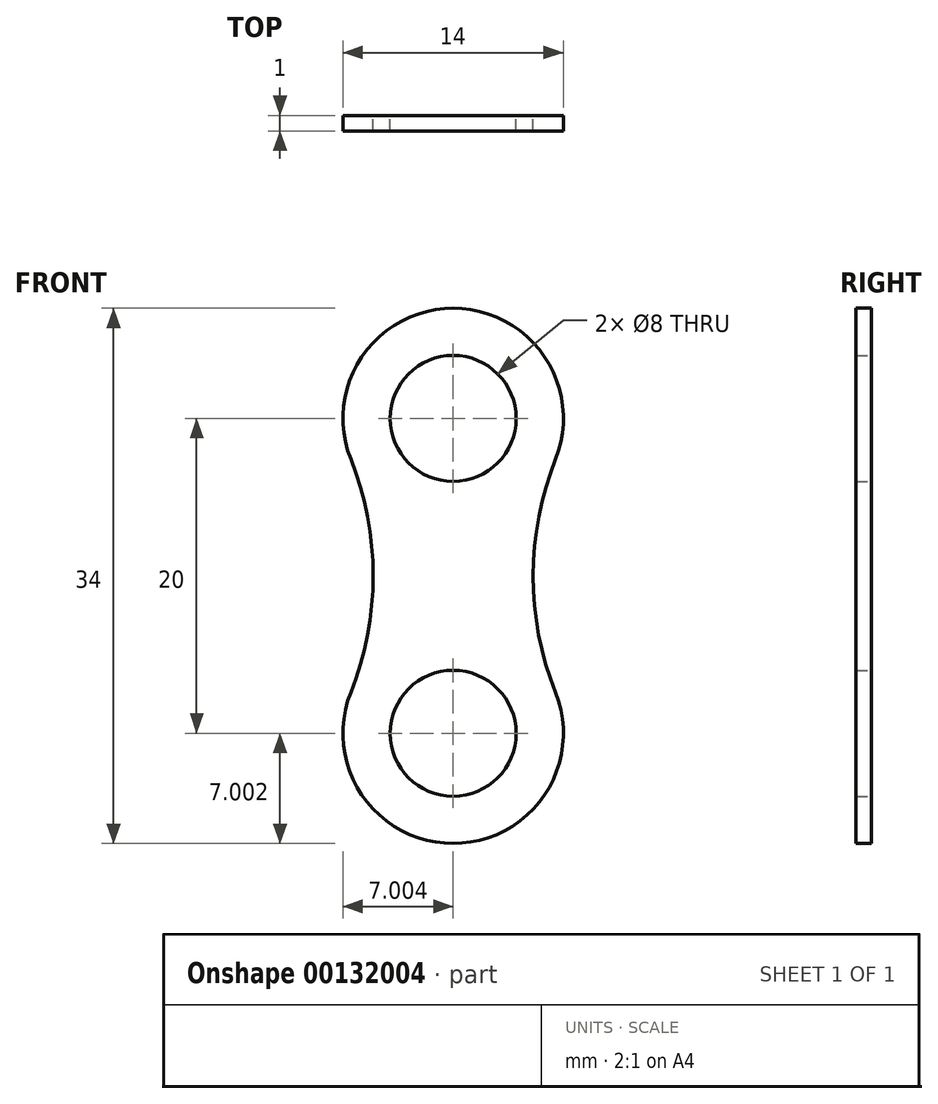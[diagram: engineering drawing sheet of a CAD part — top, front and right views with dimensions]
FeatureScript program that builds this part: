
annotation { "Feature Type Name" : "Feature", "Feature Type Description" : "" }
export const myFeature = defineFeature(function(context is Context, id is Id, definition is map)
    precondition{}
    {
        {
            var Q0;
            Q0=qCreatedBy(makeId("Front.planeOp"),FACE);
            var sketch = newSketch(context, id + "F0", { "sketchPlane" : qUnion([Q0])});
            skArc(sketch, "E0", {"start": v(-41.52, 56.14) * mm, "mid": v(-48.03, 65.73) * mm, "end": v(-54.53, 56.14) * mm});
            skArc(sketch, "E1", {"start": v(-54.53, 41.33) * mm, "mid": v(-48.03, 31.73) * mm, "end": v(-41.52, 41.33) * mm});
            skArc(sketch, "E2", {"start": v(-54.53, 41.33) * mm, "mid": v(-53.1, 48.73) * mm, "end": v(-54.53, 56.14) * mm});
            skArc(sketch, "E3", {"start": v(-41.52, 56.14) * mm, "mid": v(-42.95, 48.73) * mm, "end": v(-41.52, 41.33) * mm});
            skCircle(sketch, "E4", {"center": v(-48.03, 58.73) * mm, "radius": 4 * mm});
            skCircle(sketch, "E5", {"center": v(-48.03, 38.73) * mm, "radius": 4 * mm});
            skSolve(sketch);
        }
        {
            var Q0;
            Q0=makeQuery(id+"F0.imprint","IMPRINT",FACE,{"disambiguationData":[TD([[makeQuery(id+"F0.imprint","IMPRINT",EDGE,{"derivedFrom":sQuery(id+"F0.wireOp",EDGE,"E0")}),1.0]])]});
            extrude(context, id + "F1", {"entities" : qUnion([Q0]), "depth" : 1 * mm});
        }
    });
